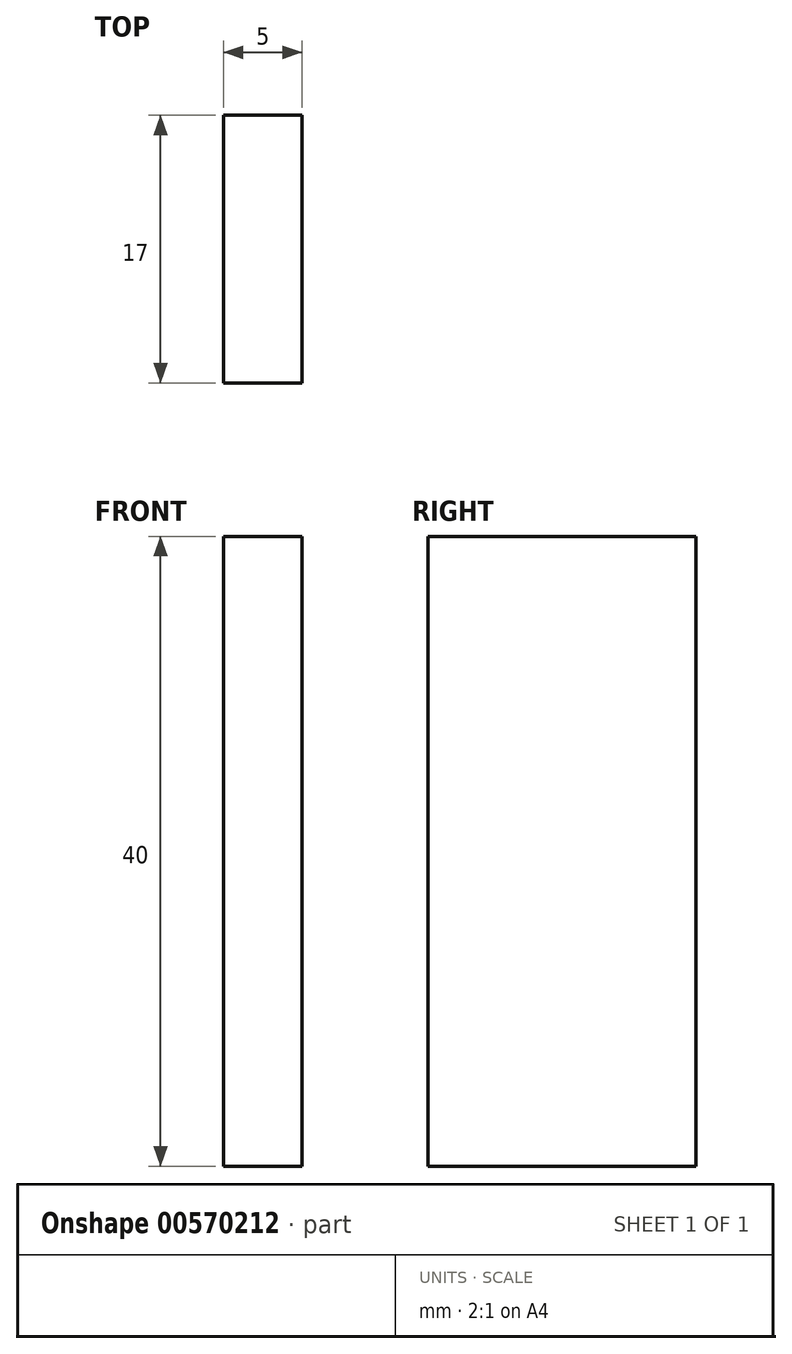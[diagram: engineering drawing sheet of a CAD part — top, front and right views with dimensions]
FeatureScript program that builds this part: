
annotation { "Feature Type Name" : "Feature", "Feature Type Description" : "" }
export const myFeature = defineFeature(function(context is Context, id is Id, definition is map)
    precondition{}
    {
        {
            var Q0;
            Q0=qCreatedBy(makeId("Front.planeOp"),FACE);
            var sketch = newSketch(context, id + "F0", { "sketchPlane" : qUnion([Q0])});
            skLineSegment(sketch, "E0.bottom", {"start": v(0, 0) * mm, "end": v(5, 0) * mm});
            skLineSegment(sketch, "E0.top", {"start": v(0, 40) * mm, "end": v(5, 40) * mm});
            skLineSegment(sketch, "E0.left", {"start": v(0, 0) * mm, "end": v(0, 40) * mm});
            skLineSegment(sketch, "E0.right", {"start": v(5, 0) * mm, "end": v(5, 40) * mm});
            skSolve(sketch);
        }
        {
            var Q0;
            Q0 = qSketchRegion(id + "F0", true);
            extrude(context, id + "F1", {"entities" : qUnion([Q0]), "depth" : 17 * mm, "offsetDistance" : 25 * mm});
        }
    });
